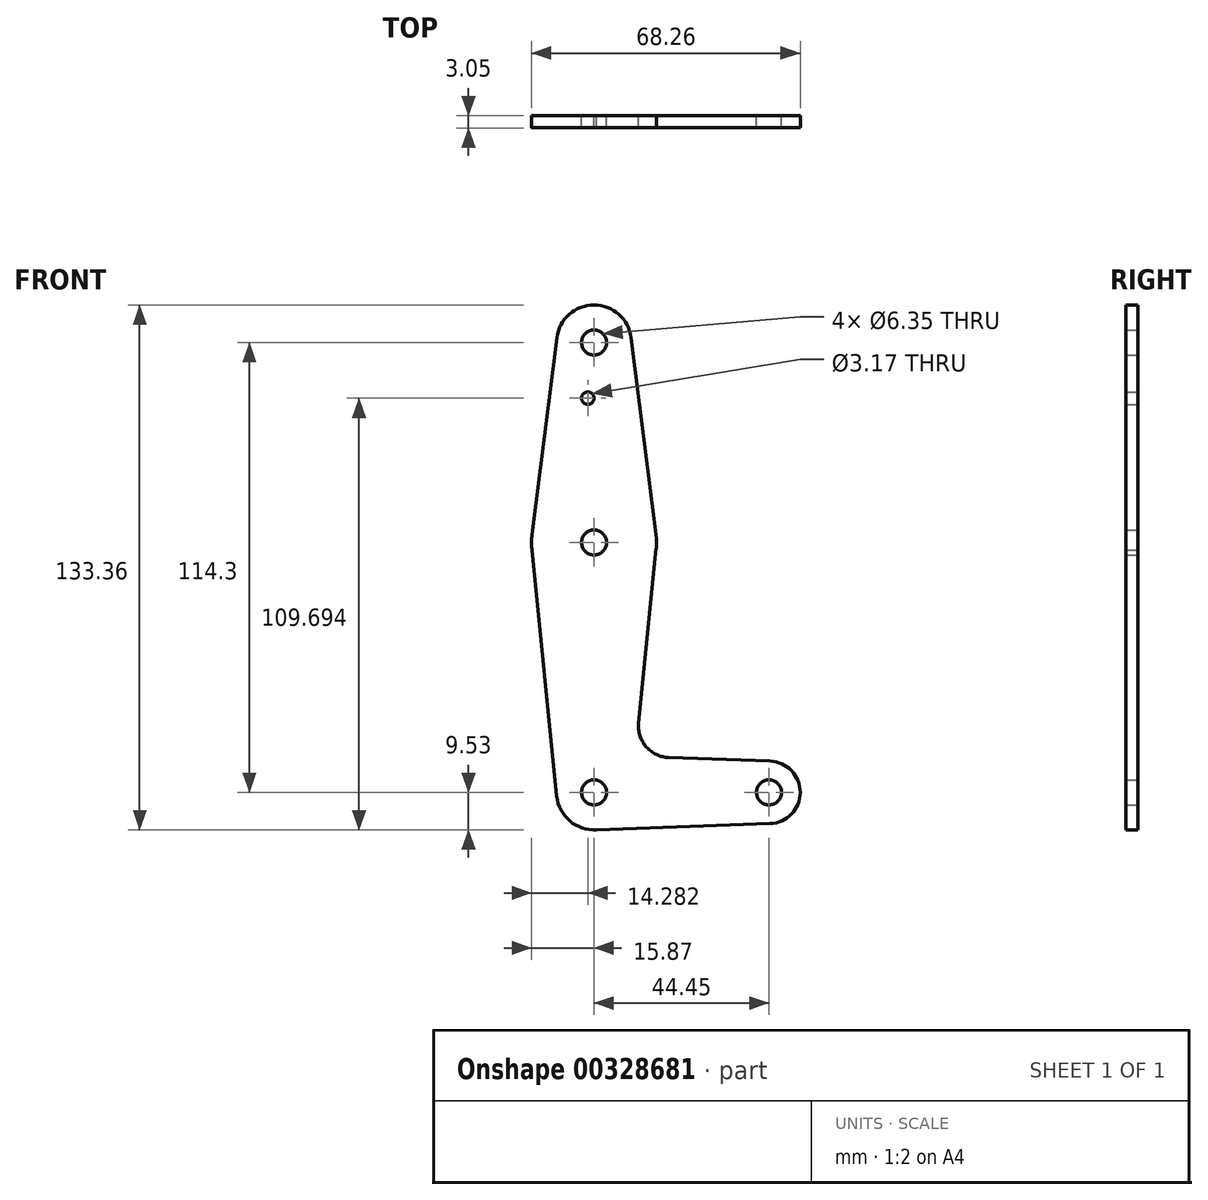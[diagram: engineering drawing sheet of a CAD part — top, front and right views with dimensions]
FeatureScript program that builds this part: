
annotation { "Feature Type Name" : "Feature", "Feature Type Description" : "" }
export const myFeature = defineFeature(function(context is Context, id is Id, definition is map)
    precondition{}
    {
        {
            var Q0;
            Q0=qCreatedBy(makeId("Front.planeOp"),FACE);
            var sketch = newSketch(context, id + "F0", { "sketchPlane" : qUnion([Q0])});
            skLineSegment(sketch, "E0", {"start": v(0, 0) * mm, "end": v(0, 114.3) * mm, "construction": true});
            skLineSegment(sketch, "E1", {"start": v(0, 0) * mm, "end": v(44.45, 0) * mm, "construction": true});
            skCircle(sketch, "E2", {"center": v(0, 114.3) * mm, "radius": 9.53 * mm});
            skCircle(sketch, "E3", {"center": v(0, 0) * mm, "radius": 9.53 * mm});
            skCircle(sketch, "E4", {"center": v(44.45, 0) * mm, "radius": 7.94 * mm});
            skCircle(sketch, "E5", {"center": v(0, 63.5) * mm, "radius": 15.88 * mm});
            skLineSegment(sketch, "E6", {"start": v(-15.75, 61.52) * mm, "end": v(-9.48, -0.95) * mm});
            skLineSegment(sketch, "E7", {"start": v(9.45, 115.5) * mm, "end": v(15.75, 65.48) * mm});
            skLineSegment(sketch, "E8", {"start": v(-9.45, 115.5) * mm, "end": v(-15.75, 65.48) * mm});
            skLineSegment(sketch, "E9", {"start": v(15.8, 61.91) * mm, "end": v(11.34, 17.6) * mm});
            skLineSegment(sketch, "E10", {"start": v(18.97, 8.85) * mm, "end": v(44.73, 7.93) * mm});
            skLineSegment(sketch, "E11", {"start": v(0, -9.53) * mm, "end": v(44.73, -7.93) * mm});
            skCircle(sketch, "E12", {"center": v(0, 114.3) * mm, "radius": 3.18 * mm});
            skCircle(sketch, "E13", {"center": v(0, 63.5) * mm, "radius": 3.18 * mm});
            skCircle(sketch, "E14", {"center": v(-1.59, 100.16) * mm, "radius": 1.59 * mm});
            skCircle(sketch, "E15", {"center": v(0, 0) * mm, "radius": 3.18 * mm});
            skCircle(sketch, "E16", {"center": v(44.45, 0) * mm, "radius": 3.18 * mm});
            skArc(sketch, "E17.filletArc", {"start": v(11.34, 17.6) * mm, "mid": v(13.26, 11.57) * mm, "end": v(18.97, 8.85) * mm});
            skSolve(sketch);
        }
        {
            var Q0;
            Q0 = qSketchRegion(id + "F0", true);
            extrude(context, id + "F1", {"entities" : qUnion([Q0]), "depth" : 3.05 * mm});
        }
    });
